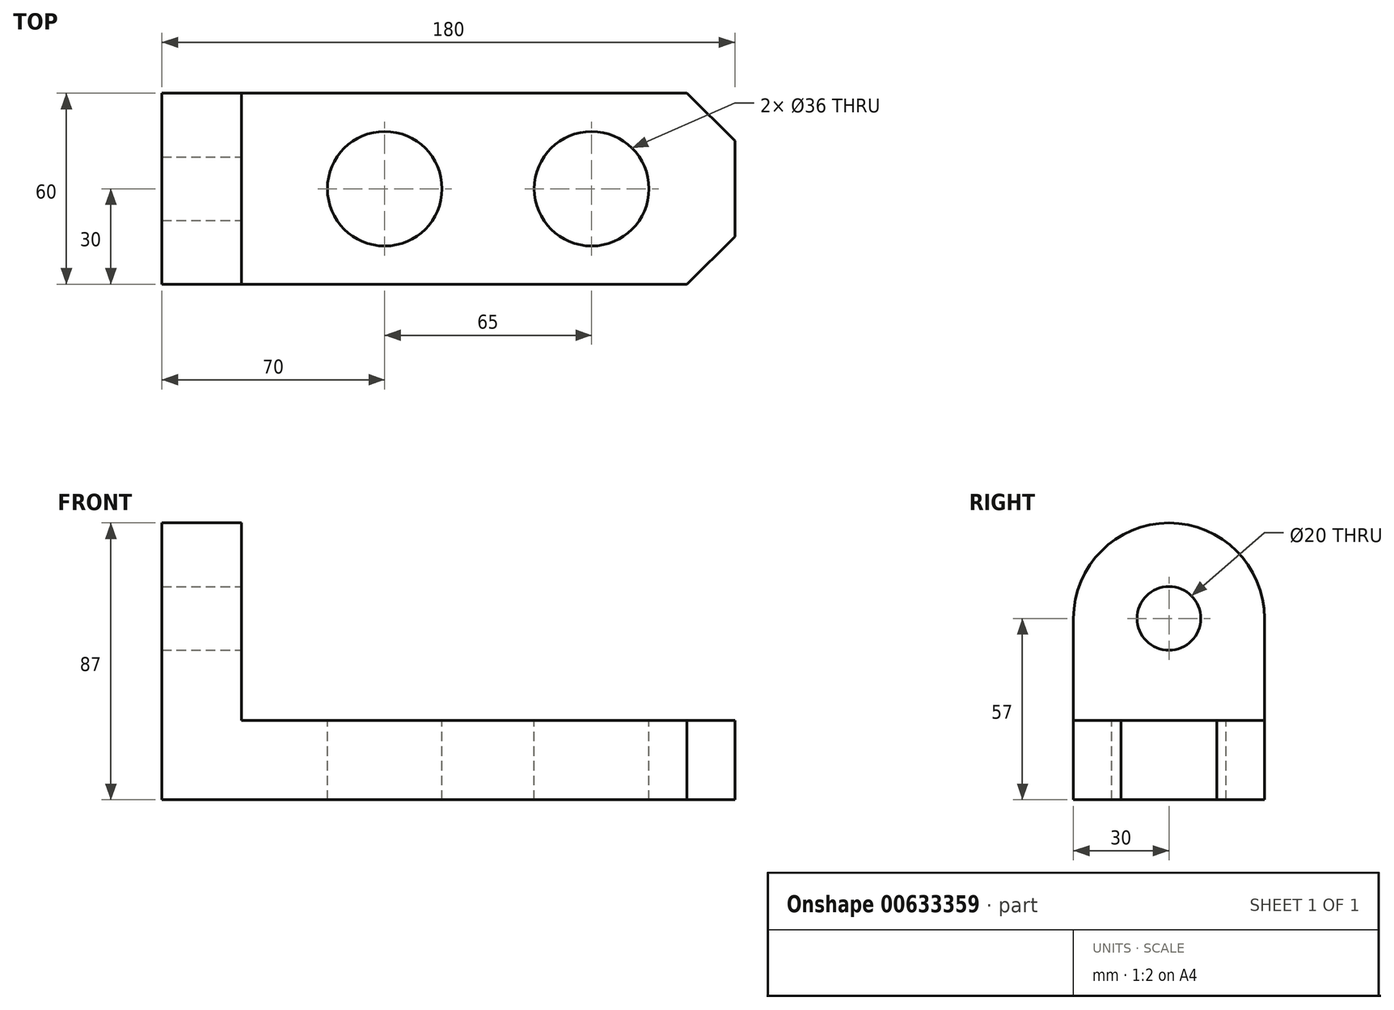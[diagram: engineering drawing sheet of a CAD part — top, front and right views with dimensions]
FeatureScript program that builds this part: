
annotation { "Feature Type Name" : "Feature", "Feature Type Description" : "" }
export const myFeature = defineFeature(function(context is Context, id is Id, definition is map)
    precondition{}
    {
        {
            var Q0;
            Q0=qCreatedBy(makeId("Top.planeOp"),FACE);
            var sketch = newSketch(context, id + "F0", { "sketchPlane" : qUnion([Q0])});
            skLineSegment(sketch, "E0.bottom", {"start": v(0, 0) * mm, "end": v(180, 0) * mm});
            skLineSegment(sketch, "E0.top", {"start": v(0, 60) * mm, "end": v(180, 60) * mm});
            skLineSegment(sketch, "E0.left", {"start": v(0, 0) * mm, "end": v(0, 60) * mm});
            skLineSegment(sketch, "E0.right", {"start": v(180, 0) * mm, "end": v(180, 60) * mm});
            skSolve(sketch);
        }
        {
            var Q0;
            Q0 = qSketchRegion(id + "F0", true);
            extrude(context, id + "F1", {"entities" : qUnion([Q0]), "depth" : 25 * mm, "offsetDistance" : 25.4 * mm});
        }
        {
            var Q0;
            Q0=makeQuery(id+"F1.opExtrude","CAP_FACE",FACE,{"disambiguationData":[OSD([sQuery(id+"F0.wireOp",EDGE,"E0.bottom"),sQuery(id+"F0.wireOp",EDGE,"E0.top"),sQuery(id+"F0.wireOp",EDGE,"E0.left"),sQuery(id+"F0.wireOp",EDGE,"E0.right")])],"isStart":false});
            var sketch = newSketch(context, id + "F2", { "sketchPlane" : qUnion([Q0])});
            skLineSegment(sketch, "E1.bottom", {"start": v(0, 60) * mm, "end": v(25, 60) * mm});
            skLineSegment(sketch, "E1.top", {"start": v(0, 0) * mm, "end": v(25, 0) * mm});
            skLineSegment(sketch, "E1.left", {"start": v(0, 60) * mm, "end": v(0, 0) * mm});
            skLineSegment(sketch, "E1.right", {"start": v(25, 60) * mm, "end": v(25, 0) * mm});
            skSolve(sketch);
        }
        {
            var Q0;
            Q0 = qSketchRegion(id + "F2", true);
            extrude(context, id + "F3", {"entities" : qUnion([Q0]), "operationType" : NewBodyOperationType.ADD, "depth" : 62 * mm, "offsetDistance" : 25.4 * mm});
        }
        {
            var Q0;
            Q0=makeQuery(id+"F3.opExtrude","CAP_EDGE",EDGE,{"disambiguationData":[OSD([sQuery(id+"F2.wireOp",EDGE,"E1.top")])],"isStart":false});
            fillet(context, id + "F4", {"entities" : qUnion([Q0]), "radius" : 30 * mm, "tangentPropagation" : true, "allowEdgeOverflow" : false});
        }
        {
            var Q0;
            Q0=makeQuery(id+"F3.opExtrude","CAP_EDGE",EDGE,{"disambiguationData":[OSD([sQuery(id+"F2.wireOp",EDGE,"E1.bottom")])],"isStart":false});
            fillet(context, id + "F5", {"entities" : qUnion([Q0]), "radius" : 30 * mm, "tangentPropagation" : true, "allowEdgeOverflow" : false});
        }
        {
            var Q0;
            Q0=makeQuery(id+"F1.opExtrude","CAP_FACE",FACE,{"disambiguationData":[OSD([sQuery(id+"F0.wireOp",EDGE,"E0.bottom"),sQuery(id+"F0.wireOp",EDGE,"E0.top"),sQuery(id+"F0.wireOp",EDGE,"E0.left"),sQuery(id+"F0.wireOp",EDGE,"E0.right")])],"isStart":false});
            var sketch = newSketch(context, id + "F6", { "sketchPlane" : qUnion([Q0])});
            skCircle(sketch, "E2", {"center": v(70, 30) * mm, "radius": 18 * mm});
            skCircle(sketch, "E3", {"center": v(135, 30) * mm, "radius": 18 * mm});
            skSolve(sketch);
        }
        {
            var Q0;
            Q0 = qSketchRegion(id + "F6", true);
            extrude(context, id + "F7", {"entities" : qUnion([Q0]), "operationType" : NewBodyOperationType.REMOVE, "oppositeDirection" : true, "depth" : 25 * mm, "offsetDistance" : 25.4 * mm});
        }
        {
            var Q0;
            Q0=makeQuery(id+"F1.opExtrude","SWEPT_EDGE",EDGE,{"disambiguationData":[OSD([sQuery(id+"F0.wireOp",EDGE,"E0.bottom"),sQuery(id+"F0.wireOp",EDGE,"E0.right")])]});
            var Q1;
            Q1=makeQuery(id+"F1.opExtrude","SWEPT_EDGE",EDGE,{"disambiguationData":[OSD([sQuery(id+"F0.wireOp",EDGE,"E0.top"),sQuery(id+"F0.wireOp",EDGE,"E0.right")])]});
            chamfer(context, id + "F8", {"entities" : qUnion([Q0, Q1]), "width" : 15 * mm, "tangentPropagation" : true});
        }
        {
            var Q0;
            Q0=makeQuery(id+"F3.opExtrude","SWEPT_FACE",FACE,{"disambiguationData":[OSD([sQuery(id+"F2.wireOp",EDGE,"E1.right")])]});
            var sketch = newSketch(context, id + "F9", { "sketchPlane" : qUnion([Q0])});
            skCircle(sketch, "E4", {"center": v(30, 57) * mm, "radius": 10 * mm});
            skSolve(sketch);
        }
        {
            var Q0;
            Q0 = qSketchRegion(id + "F9", true);
            extrude(context, id + "F10", {"entities" : qUnion([Q0]), "operationType" : NewBodyOperationType.REMOVE, "endBound" : BoundingType.THROUGH_ALL, "oppositeDirection" : true, "depth" : 25.4 * mm, "offsetDistance" : 25.4 * mm});
        }
    });
